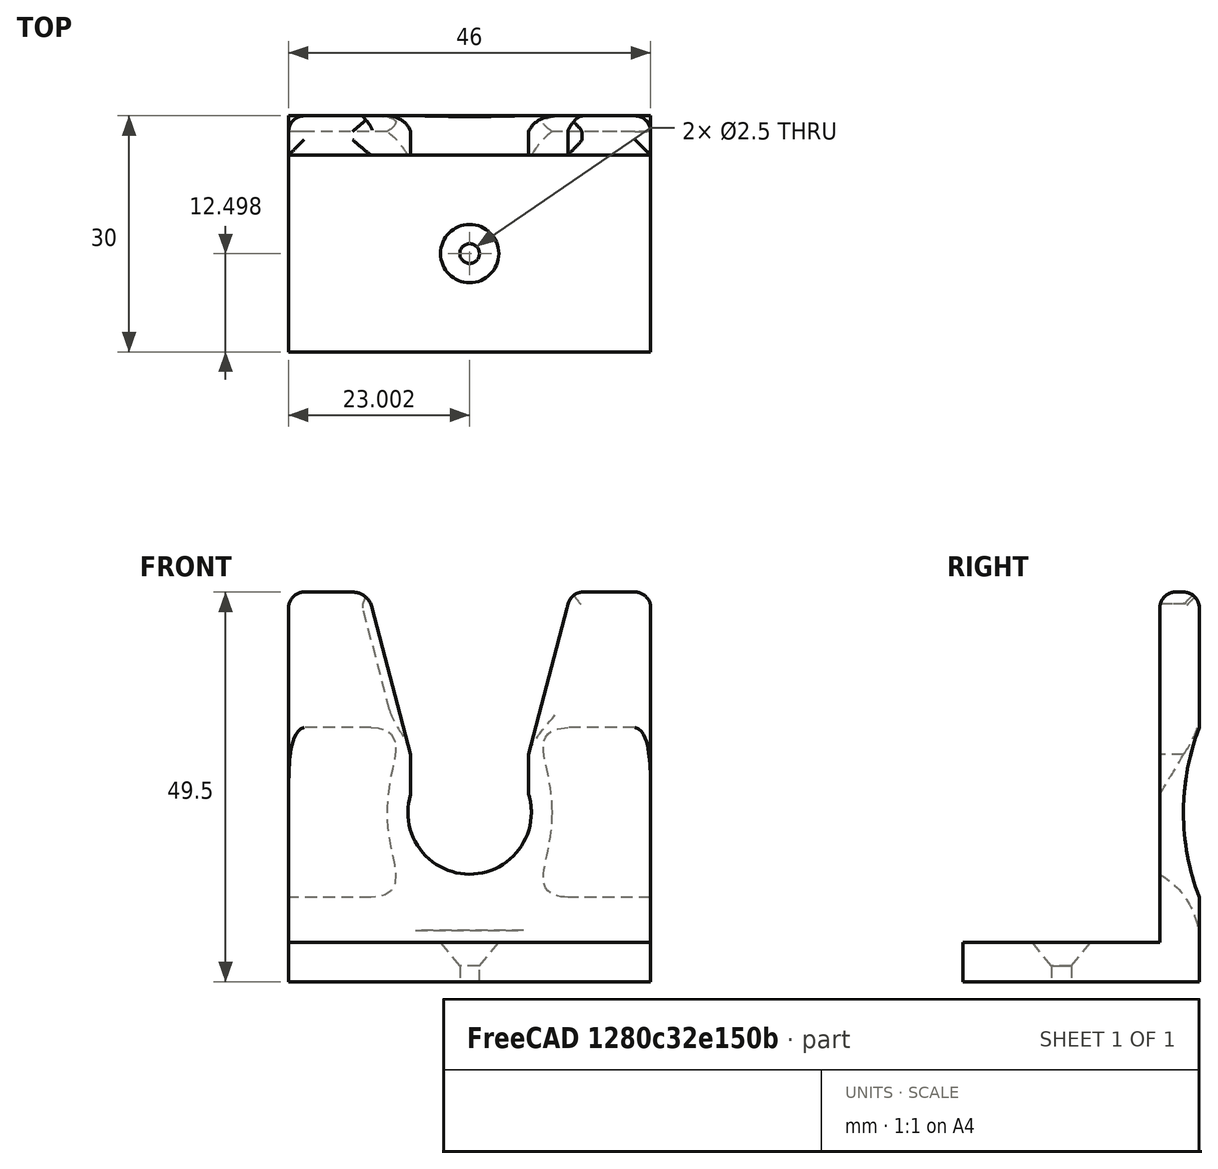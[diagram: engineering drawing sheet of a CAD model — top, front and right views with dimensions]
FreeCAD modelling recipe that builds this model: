
FCSTD DOCUMENT  (FreeCAD 0.18.4R)
Label: Borotva.Tarto
License: All rights reserved
LicenseURL: http://en.wikipedia.org/wiki/All_rights_reserved
objects: Part::Cut×9, Part::Part2DObjectPython×8, Part::Extrusion×7, Part::FeaturePython×5, Part::MultiFuse×3, Part::Feature×3, App::DocumentObjectGroup×2
note: 35 computed .brp shape members not serialized (recipe doc carries the construction recipe); baked Part::Feature solids carry a one-line shape summary decoded from their .brp

FEATURE [Part::Part2DObjectPython] Rectangle024  # Draft 2D object (typed FeaturePython)
  ChamferSize = 0
  Columns = 1
  FilletRadius = 0
  Height = 10
  Length = 30
  MakeFace = true
  Placement = pos=(-209.234,-607.175,22) rot=(0.675329,0.521503,0.521503;1.95364rad)
  Rows = 1
FEATURE [Part::FeaturePython] Slice001  # WARN: FeaturePython — macro-defined, semantics opaque (R4)
  Mode = 1
  Tolerance = 0
  Tools = -> [Rectangle024]
FEATURE [Part::FeaturePython] Slice001_child0  label="Slice001.0"  # WARN: FeaturePython — macro-defined, semantics opaque (R4)
  Base = -> Slice001
  FilterType = 1
  Invert = false
  OverrideMaxVal = 0
  WindowFrom = 80
  WindowTo = 100
  items = 0
FEATURE [Part::Part2DObjectPython] Rectangle030  # Draft 2D object (typed FeaturePython)
  ChamferSize = 0
  Columns = 1
  FilletRadius = 0
  Height = 2
  Length = 2
  MakeFace = true
  Placement = pos=(-177.952,-611.418,27) rot=(0.983879,0.126455,0.126455;1.58705rad)
  Rows = 1
FEATURE [Part::Extrusion] Extrusion
  Base = -> Rectangle030
  Dir = (-10.4714,40.0633,-3.856e-13)
  DirMode = 0
  FaceMakerClass = Part::FaceMakerBullseye
  LengthFwd = 0
  LengthRev = 0
  Solid = true
  Symmetric = false
FEATURE [Part::Part2DObjectPython] Rectangle031  # Draft 2D object (typed FeaturePython)
  ChamferSize = 0
  Columns = 1
  FilletRadius = 0
  Height = 2
  Length = 2
  MakeFace = true
  Placement = pos=(-209.335,-607.562,27.1864) rot=(0.09051,0.704205,0.704205;2.96107rad)
  Rows = 1
FEATURE [Part::Extrusion] Extrusion001
  Base = -> Rectangle031
  Dir = (8.92673,34.1533,2.1e-15)
  DirMode = 0
  FaceMakerClass = Part::FaceMakerBullseye
  LengthFwd = 0
  LengthRev = 0
  Solid = true
  Symmetric = false
FEATURE [Part::Part2DObjectPython] Circle  # Draft 2D object (typed FeaturePython)
  FirstAngle = 0
  LastAngle = 0
  MakeFace = true
  Placement = pos=(-211.27,-607.056,27.1864) rot=(0.09051,0.704205,0.704205;2.96107rad)
  Radius = 2
FEATURE [Part::Extrusion] Extrusion002
  Base = -> Circle
  Dir = (8.92673,34.1533,2.1e-15)
  DirMode = 0
  FaceMakerClass = Part::FaceMakerBullseye
  LengthFwd = 0
  LengthRev = 0
  Solid = true
  Symmetric = false
FEATURE [Part::Cut] Cut
  Base = -> Extrusion001
  Tool = -> Extrusion002
FEATURE [Part::Cut] Cut001
  Base = -> Slice001_child0
  Tool = -> Cut
FEATURE [Part::Part2DObjectPython] Circle001  # Draft 2D object (typed FeaturePython)
  FirstAngle = 0
  LastAngle = 0
  MakeFace = true
  Placement = pos=(-176.017,-610.912,27) rot=(0.983879,0.126455,0.126455;1.58705rad)
  Radius = 2
FEATURE [Part::Extrusion] Extrusion003
  Base = -> Circle001
  Dir = (-10.4714,40.0633,-3.856e-13)
  DirMode = 0
  FaceMakerClass = Part::FaceMakerBullseye
  LengthFwd = 0
  LengthRev = 0
  Solid = true
  Symmetric = false
FEATURE [Part::Cut] Cut002
  Base = -> Extrusion
  Tool = -> Extrusion003
FEATURE [Part::Cut] Cut003
  Base = -> Cut001
  Tool = -> Cut002
FEATURE [Part::Cut] Cut006
FEATURE [Part::Part2DObjectPython] Circle006  # Draft 2D object (typed FeaturePython)
  FirstAngle = 0
  LastAngle = 0
  MakeFace = true
  Placement = pos=(-179.691,-596.813,36.981) rot=(0,0,1;0rad)
  Radius = 2
FEATURE [Part::Part2DObjectPython] Wire004  # Draft 2D object (typed FeaturePython)
  ChamferSize = 0
  Closed = true
  End = (-179.691,-598.813,36.981)
  FilletRadius = 0
  Length = 12.8553
  MakeFace = true
  Placement = pos=(-182.544,-602.772,36.981) rot=(0,0,1;0rad)
  Points = (3) [(0,0,0),(0.917468,5.45383,-1.42109e-14),(2.85246,3.95959,0)]
  Start = (-182.544,-602.772,36.981)
  Subdivisions = 0
  Support = -> [Circle006]
FEATURE [Part::Extrusion] Extrusion010
  Base = -> Wire004
  Dir = (9.42e-14,7.64e-14,-19.962)
  DirMode = 0
  FaceMakerClass = Part::FaceMakerBullseye
  LengthFwd = 0
  LengthRev = 0
  Solid = true
  Symmetric = false
FEATURE [Part::Extrusion] Extrusion011
  Base = -> Circle006
  Dir = (0,1.442e-13,-19.962)
  DirMode = 0
  FaceMakerClass = Part::FaceMakerBullseye
  LengthFwd = 0
  LengthRev = 0
  Solid = true
  Symmetric = false
FEATURE [Part::Cut] Cut008
  Base = -> Extrusion010
  Tool = -> Extrusion011
FEATURE [Part::Cut] Cut009
  Base = -> Cut003
  Tool = -> Cut008
FEATURE [Part::Cut] Cut010
  Base = -> Cut009
  Tool = -> Cut006
FEATURE [App::DocumentObjectGroup] GrExplode_Slice001001  label="Exploded Slice002"
  Group = -> [Cut010]
FEATURE [Part::Part2DObjectPython] Rectangle  # Draft 2D object (typed FeaturePython)
  ChamferSize = 0
  Columns = 1
  FilletRadius = 0
  Height = 74.5955
  Length = 92.0788
  MakeFace = true
  Placement = pos=(-217.148,-623.897,29) rot=(0,0,1;0rad)
  Rows = 1
  Support = -> [Cut010]
FEATURE [Part::FeaturePython] Slice  # WARN: FeaturePython — macro-defined, semantics opaque (R4)
  Base = -> Cut010
  Mode = 1
  Tolerance = 0
  Tools = -> [Rectangle]
FEATURE [Part::FeaturePython] Slice_child0  label="Slice.0"  # WARN: FeaturePython — macro-defined, semantics opaque (R4)
  Base = -> Slice
  FilterType = 1
  Invert = false
  OverrideMaxVal = 0
  WindowFrom = 80
  WindowTo = 100
  items = 0
FEATURE [Part::FeaturePython] Slice_child1  label="Slice.1"  # WARN: FeaturePython — macro-defined, semantics opaque (R4)
  Base = -> Slice
  FilterType = 1
  Invert = false
  OverrideMaxVal = 0
  Placement = pos=(0,0,-30) rot=(0,0,1;0rad)
  WindowFrom = 80
  WindowTo = 100
  items = 1
FEATURE [Part::MultiFuse] Fusion
  Placement = pos=(0,-553.302,-555.302) rot=(-1,0,0;1.5708rad)
  Shapes = -> [Slice_child0,Slice_child1]
FEATURE [Part::Feature] Face001
  Placement = pos=(0,-583.302,-555.302) rot=(-1,0,0;1.5708rad)
  shape: bbox 38.98 x 20 x 2e-07 mm, 1 faces, 0 solids (baked)
FEATURE [Part::Extrusion] Extrusion012
  Base = -> Face001
  Dir = (0,-3e-16,-1.5)
  DirMode = 0
  FaceMakerClass = Part::FaceMakerBullseye
  LengthFwd = 0
  LengthRev = 0
  Solid = true
  Symmetric = false
FEATURE [Part::MultiFuse] Fusion001
  Shapes = -> [Fusion,Extrusion012]
FEATURE [Part::MultiFuse] Fusion002
  Placement = pos=(-46,0,1.8e-15) rot=(0,0,1;0rad)
  Shapes = -> [Extrusion012]
FEATURE [Part::Cut] Cut011
  Base = -> Fusion001
  Tool = -> Fusion002
FEATURE [App::DocumentObjectGroup] GrExplode_Slice  label="Exploded Slice"
  Group = -> [Cut011]
FEATURE [Part::Feature] Cut011_solid  label="Cut011 (Solid)"
  shape: bbox 51.09 x 30 x 53.54 mm, 53 faces (baked)
FEATURE [Part::Feature] Cut011_solid001  label="Borotva.Tarto"
  shape: bbox 51.09 x 30 x 53.54 mm, 37 faces (baked)
